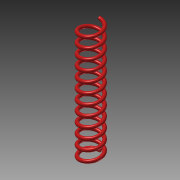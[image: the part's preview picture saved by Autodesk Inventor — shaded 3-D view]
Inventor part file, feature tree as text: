
AUTODESK INVENTOR PART (.ipt)
format: ipt  version: 2014 (Build 180170000, 170)  size: 500,736 bytes
history: native  units: mm
features: helix x1, sketch x1
ambient origin geometry x8: Origin, YZ Plane, XZ Plane, XY Plane, X Axis, Y Axis, Z Axis, Center Point
bodies: Solid1 (feature_tree)
feature tree (2):
  helix  "Coil1"  [1 undecoded]
  sketch  "Sketch2"  dims[d1=1.0mm d2=3.0mm d3=34.925mm d4=10.0mm d5=0.0mm d6=90.0deg d7=90.0deg d8=0.0mm d9=0.0mm]
note: 1 required parameter value undecoded (feature->parameter linkage not recoverable at this tier; creation-order binding heuristic only, values carry confidence <= 0.55)
